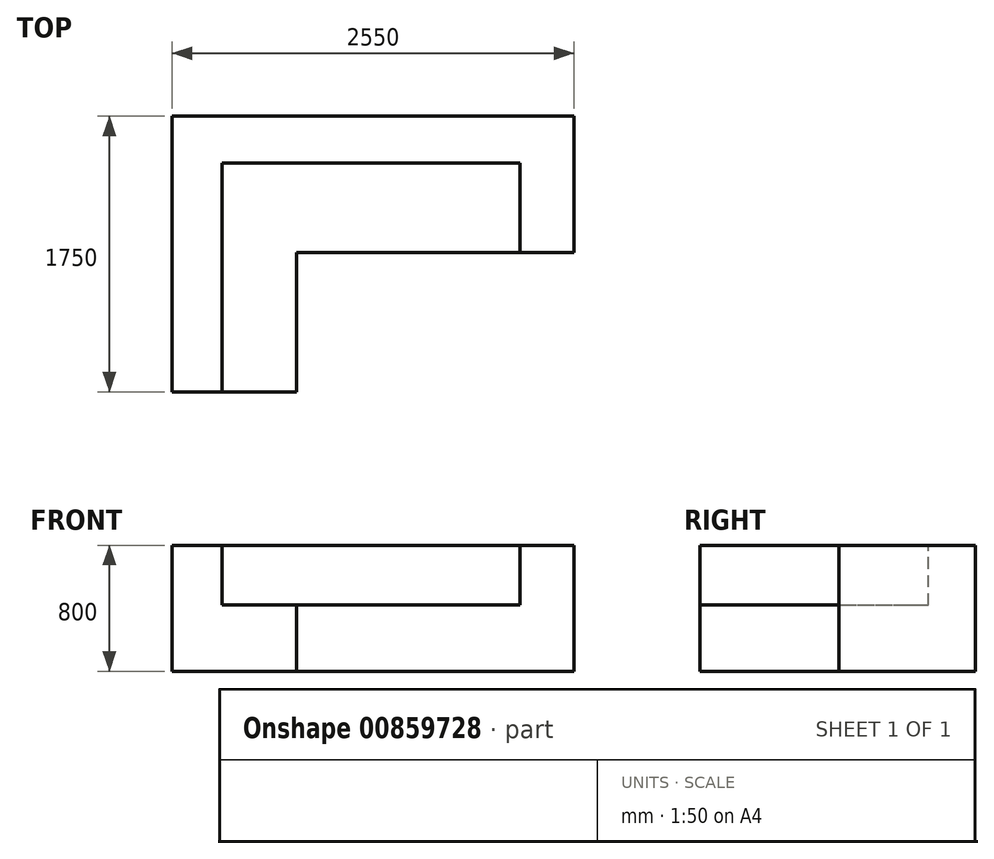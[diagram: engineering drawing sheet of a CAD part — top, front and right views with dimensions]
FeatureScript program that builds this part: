
annotation { "Feature Type Name" : "Feature", "Feature Type Description" : "" }
export const myFeature = defineFeature(function(context is Context, id is Id, definition is map)
    precondition{}
    {
        {
            var Q0;
            Q0=qCreatedBy(makeId("Right.planeOp"),FACE);
            var sketch = newSketch(context, id + "F0", { "sketchPlane" : qUnion([Q0])});
            skLineSegment(sketch, "E0.bottom", {"start": v(-953.03, 800) * mm, "end": v(796.97, 800) * mm});
            skLineSegment(sketch, "E0.top", {"start": v(-953.03, 0) * mm, "end": v(796.97, 0) * mm});
            skLineSegment(sketch, "E0.left", {"start": v(-953.03, 800) * mm, "end": v(-953.03, 0) * mm});
            skLineSegment(sketch, "E0.right", {"start": v(796.97, 800) * mm, "end": v(796.97, 0) * mm});
            skSolve(sketch);
        }
        {
            var Q0;
            Q0=makeQuery(id+"F0.imprint","IMPRINT",FACE,{"disambiguationData":[TD([[makeQuery(id+"F0.imprint","IMPRINT",EDGE,{"derivedFrom":sQuery(id+"F0.wireOp",EDGE,"E0.bottom")}),-1.0]])]});
            extrude(context, id + "F1", {"entities" : qUnion([Q0]), "depth" : 2550 * mm, "offsetDistance" : 25 * mm});
        }
        {
            var Q0;
            Q0=makeQuery(id+"F1.opExtrude","SWEPT_FACE",FACE,{"disambiguationData":[OSD([sQuery(id+"F0.wireOp",EDGE,"E0.bottom")])]});
            var sketch = newSketch(context, id + "F2", { "sketchPlane" : qUnion([Q0])});
            skLineSegment(sketch, "E1.bottom", {"start": v(2550, -953.03) * mm, "end": v(790.05, -953.03) * mm});
            skLineSegment(sketch, "E1.top", {"start": v(2550, -68) * mm, "end": v(790.05, -68) * mm});
            skLineSegment(sketch, "E1.left", {"start": v(2550, -953.03) * mm, "end": v(2550, -68) * mm});
            skLineSegment(sketch, "E1.right", {"start": v(790.05, -953.03) * mm, "end": v(790.05, -68) * mm});
            skSolve(sketch);
        }
        {
            var Q0;
            Q0 = qSketchRegion(id + "F2", true);
            extrude(context, id + "F3", {"entities" : qUnion([Q0]), "operationType" : NewBodyOperationType.REMOVE, "oppositeDirection" : true, "depth" : 940 * mm, "offsetDistance" : 25 * mm});
        }
        {
            var Q0;
            Q0=makeQuery(id+"F1.opExtrude","SWEPT_FACE",FACE,{"disambiguationData":[OSD([sQuery(id+"F0.wireOp",EDGE,"E0.bottom")])]});
            var sketch = newSketch(context, id + "F4", { "sketchPlane" : qUnion([Q0])});
            skLineSegment(sketch, "E2.top", {"start": v(2208.03, 499.94) * mm, "end": v(790.05, 499.94) * mm});
            skLineSegment(sketch, "E2.left", {"start": v(2208.03, -68) * mm, "end": v(2208.03, 499.94) * mm});
            skLineSegment(sketch, "E3.top", {"start": v(790.05, 499.94) * mm, "end": v(316.13, 499.94) * mm});
            skLineSegment(sketch, "E3.right", {"start": v(316.13, -953.03) * mm, "end": v(316.13, 499.94) * mm});
            skLineSegment(sketch, "E4", {"start": v(316.13, -953.03) * mm, "end": v(790.05, -953.03) * mm});
            skLineSegment(sketch, "E5", {"start": v(790.05, -953.03) * mm, "end": v(790.05, -68) * mm});
            skLineSegment(sketch, "E6", {"start": v(790.05, -68) * mm, "end": v(2208.03, -68) * mm});
            skSolve(sketch);
        }
        {
            var Q0;
            Q0 = qSketchRegion(id + "F4", true);
            extrude(context, id + "F5", {"entities" : qUnion([Q0]), "operationType" : NewBodyOperationType.REMOVE, "oppositeDirection" : true, "depth" : 380 * mm, "offsetDistance" : 25 * mm});
        }
    });
